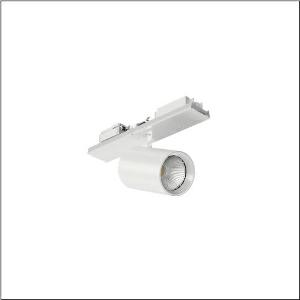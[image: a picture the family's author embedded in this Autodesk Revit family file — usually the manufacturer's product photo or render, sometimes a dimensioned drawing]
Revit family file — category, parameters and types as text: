
# Revit family: licross_r__spot_31_51sl13da43b_6d5a
name_source: partatom
category: Lighting Fixtures
units: mm (PartAtom-declared; Revit-internal decimal feet)

## family parameters
Cut with Voids When Loaded = No
Host = Face
Light Source = No
Part Type = Normal
Room Calculation Point = No
Round Connector Dimension = Use Diameter
Shared = No

## types (1)
- --- (1 x LED, 3680 lm, 28.6 W, 4000K)
    Apparent Load = 29 VA
    CIE Flux Codes = 92 97 99 100 100
    Color Rendering = 90
    Color Temperature = 4000K
    Default Elevation = 1800 mm
    Description = Licross® Spot 31, directional spotlight, light control with lens, of plastic, LED rated luminous flux: 3.680lm, light colour: 940, with plug, 5-pole, mains connection: 220..240V, AC, 50/60Hz, of aluminium, traffic white (RAL 9016), length: 140mm, diameter: 90mm, protection rating (complete): IP20, insulation class (complete): insulation class I (protective earthing), certification: CE, packaging unit: 1 piece
    Height = 175 mm
    Lamp = 1 x LED
    Lamp Light Flux = 3680 lm
    Lamp Power = 28.6 W
    Lamp count = 1
    Length = 90 mm
    Luminous efficacy = 129 lm/W
    Manufacturer = Siteco
    ModVariant = No
    Model = 51SL13DA43B
    Mounting Place = Ceiling
    Mounting Type = Pendant
    Number of Poles = 1
    OnlyDefault = Yes
    Power Factor = 1
    Product Name = Licross® Spot 31
    Product group = directional spotlight
    ProductGroupID = 905
    Protection Class = Protection class I
    Protection Degree = IP 20
    RLX_Detail_Level = 1
    RLX_Emergency_Light_Flux = 0 lm
    RLX_Emergency_Type = 0
    RLX_Emergency_Type_DB = No
    RlxData = <blob elided: 14797 chars, md5=df1b93d4>
    Socket = socket
    Standby Power = 0 W
    System Light Flux = 3680 lm
    System Power = 29 W
    Type Comments = factory setting: luminous flux: 100 % | (ON | ON | ON) | 700 mA
    Type Image = l_1245720.jpg
    URL = http://relux.com
    VarID = @adj_063831
    Voltage = 0 V
    Weight = 0.00 kg
    Width = 0 mm  [stored 0 ft]

note: [stored X ft] marks values corroborated as IEEE doubles in the binary element streams (Revit-internal decimal feet)

## geometry (parser evidence)
native form markers: Sweep x10
no freeform markers — native parametric forms only
